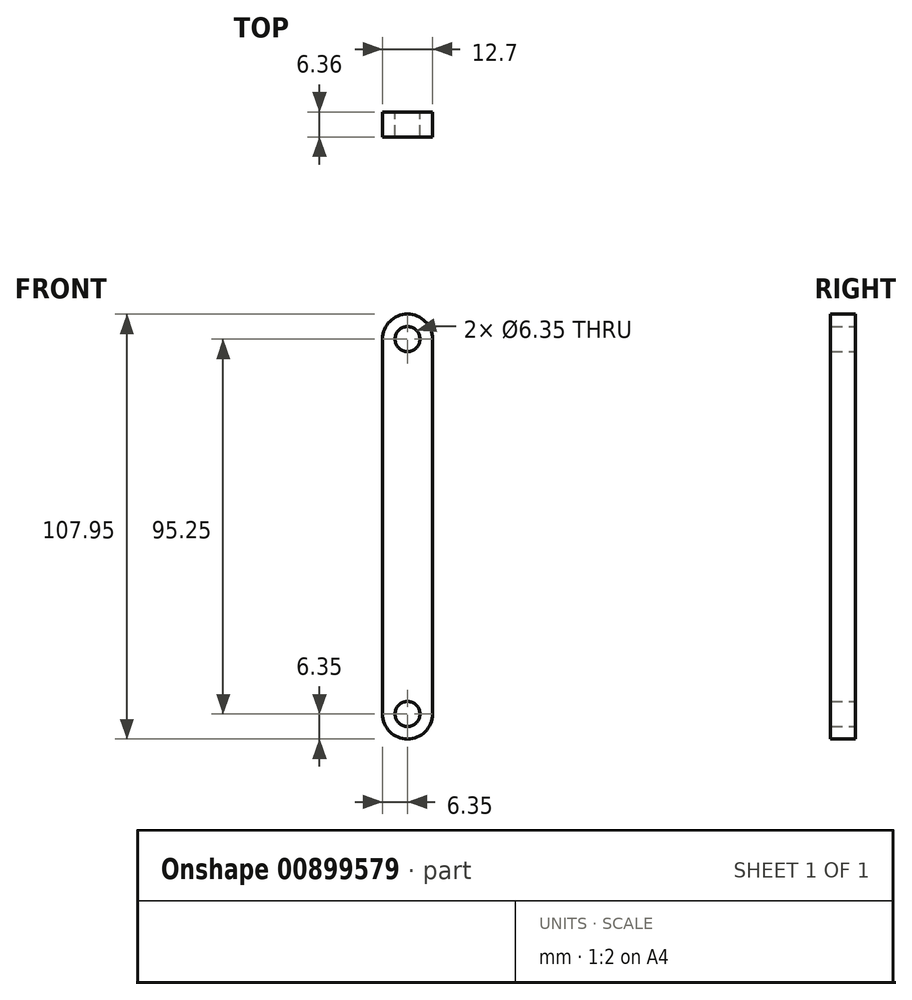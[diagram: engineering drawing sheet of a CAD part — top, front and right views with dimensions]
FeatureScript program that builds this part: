
annotation { "Feature Type Name" : "Feature", "Feature Type Description" : "" }
export const myFeature = defineFeature(function(context is Context, id is Id, definition is map)
    precondition{}
    {
        {
            var Q0;
            Q0=qCreatedBy(makeId("Front.planeOp"),FACE);
            var sketch = newSketch(context, id + "F0", { "sketchPlane" : qUnion([Q0])});
            skLineSegment(sketch, "E0", {"start": v(-6.35, 0) * mm, "end": v(-6.35, -95.25) * mm});
            skLineSegment(sketch, "E1", {"start": v(6.35, 0) * mm, "end": v(6.35, -95.25) * mm});
            skArc(sketch, "E2", {"start": v(-6.35, -95.25) * mm, "mid": v(0, -101.6) * mm, "end": v(6.35, -95.25) * mm});
            skArc(sketch, "E3", {"start": v(6.35, 0) * mm, "mid": v(0, 6.35) * mm, "end": v(-6.35, 0) * mm});
            skCircle(sketch, "E4", {"center": v(0, 0) * mm, "radius": 3.18 * mm});
            skCircle(sketch, "E5", {"center": v(0, -95.25) * mm, "radius": 3.18 * mm});
            skSolve(sketch);
        }
        {
            var Q0;
            Q0=makeQuery(id+"F0.imprint","IMPRINT",FACE,{"disambiguationData":[TD([[makeQuery(id+"F0.imprint","IMPRINT",EDGE,{"derivedFrom":sQuery(id+"F0.wireOp",EDGE,"E0")}),1.0]])]});
            extrude(context, id + "F1", {"entities" : qUnion([Q0]), "endBound" : BoundingType.SYMMETRIC, "depth" : 6.35 * mm, "offsetDistance" : 25.4 * mm});
        }
    });
